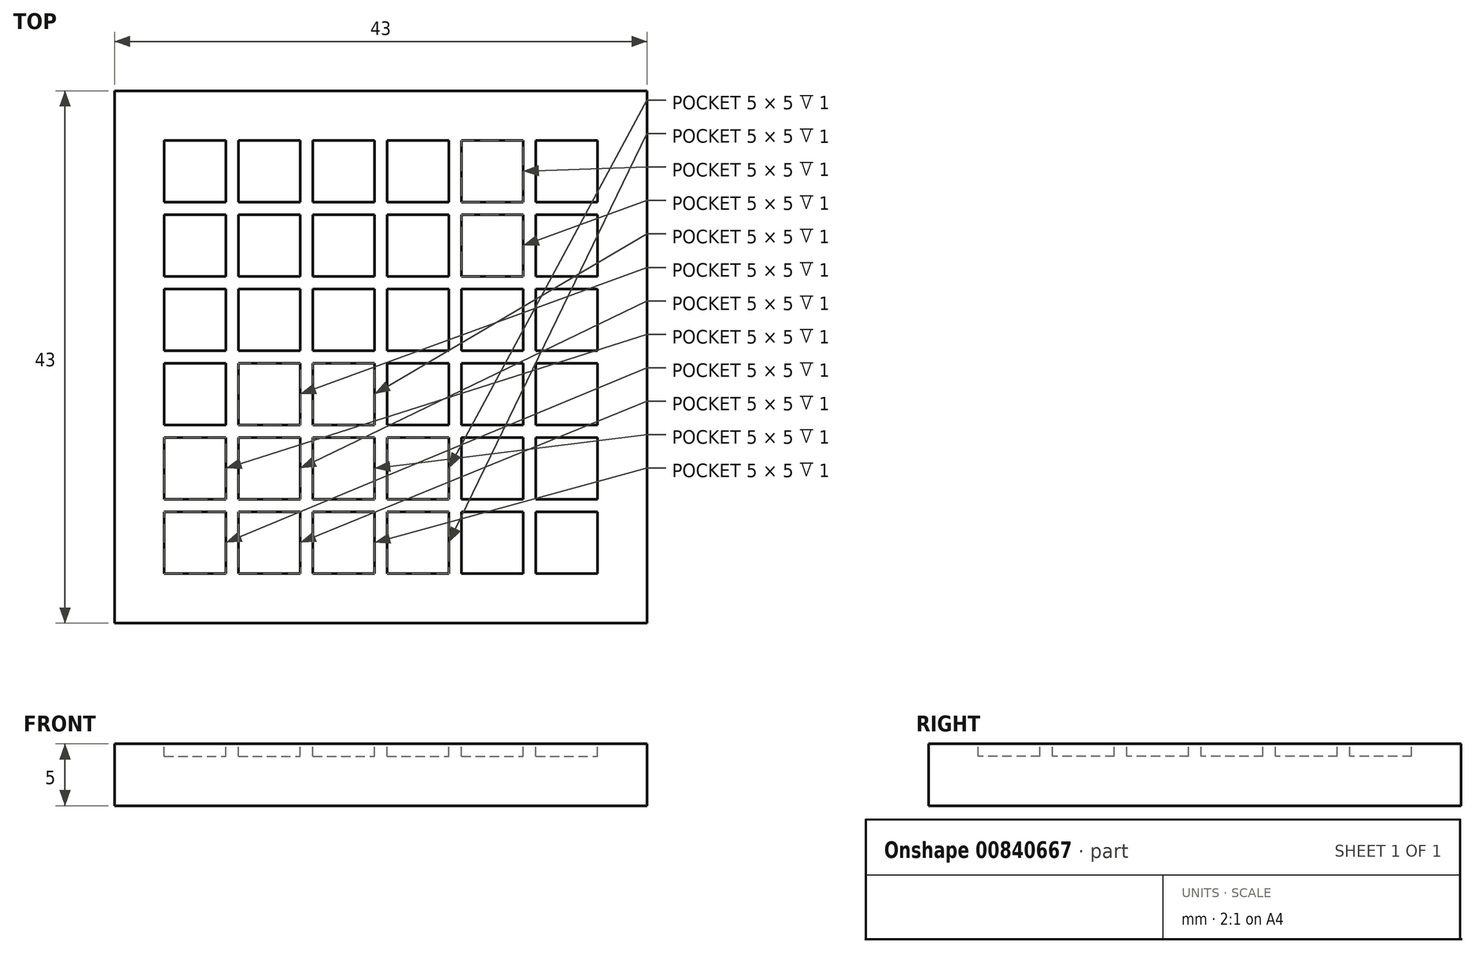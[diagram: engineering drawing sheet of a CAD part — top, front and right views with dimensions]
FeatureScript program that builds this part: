
annotation { "Feature Type Name" : "Feature", "Feature Type Description" : "" }
export const myFeature = defineFeature(function(context is Context, id is Id, definition is map)
    precondition{}
    {
        {
            var Q0;
            Q0=qCreatedBy(makeId("Top.planeOp"),FACE);
            var sketch = newSketch(context, id + "F0", { "sketchPlane" : qUnion([Q0])});
            skLineSegment(sketch, "E0.bottom", {"start": v(0, 0) * mm, "end": v(43, 0) * mm});
            skLineSegment(sketch, "E0.top", {"start": v(0, -43) * mm, "end": v(43, -43) * mm});
            skLineSegment(sketch, "E0.left", {"start": v(0, 0) * mm, "end": v(0, -43) * mm});
            skLineSegment(sketch, "E0.right", {"start": v(43, 0) * mm, "end": v(43, -43) * mm});
            skSolve(sketch);
        }
        {
            var Q0;
            Q0=makeQuery(id+"F0.imprint","IMPRINT",FACE,{"disambiguationData":[TD([[makeQuery(id+"F0.imprint","IMPRINT",EDGE,{"derivedFrom":sQuery(id+"F0.wireOp",EDGE,"E0.bottom")}),-1.0]])]});
            extrude(context, id + "F1", {"entities" : qUnion([Q0]), "depth" : 5 * mm, "offsetDistance" : 25 * mm});
        }
        {
            var Q0;
            Q0=makeQuery(id+"F1.opExtrude","CAP_FACE",FACE,{"disambiguationData":[OSD([sQuery(id+"F0.wireOp",EDGE,"E0.bottom"),sQuery(id+"F0.wireOp",EDGE,"E0.top"),sQuery(id+"F0.wireOp",EDGE,"E0.left"),sQuery(id+"F0.wireOp",EDGE,"E0.right")])],"isStart":false});
            var sketch = newSketch(context, id + "F2", { "sketchPlane" : qUnion([Q0])});
            skLineSegment(sketch, "E1.bottom", {"start": v(4, -4) * mm, "end": v(9, -4) * mm});
            skLineSegment(sketch, "E1.top", {"start": v(4, -9) * mm, "end": v(9, -9) * mm});
            skLineSegment(sketch, "E1.left", {"start": v(4, -4) * mm, "end": v(4, -9) * mm});
            skLineSegment(sketch, "E1.right", {"start": v(9, -4) * mm, "end": v(9, -9) * mm});
            skLineSegment(sketch, "E2.0.1.0", {"start": v(4, -15) * mm, "end": v(9, -15) * mm});
            skLineSegment(sketch, "E2.0.1.1", {"start": v(9, -10) * mm, "end": v(9, -15) * mm});
            skLineSegment(sketch, "E2.0.1.2", {"start": v(4, -10) * mm, "end": v(4, -15) * mm});
            skLineSegment(sketch, "E2.0.1.3", {"start": v(4, -10) * mm, "end": v(9, -10) * mm});
            skLineSegment(sketch, "E2.0.2.0", {"start": v(4, -21) * mm, "end": v(9, -21) * mm});
            skLineSegment(sketch, "E2.0.2.1", {"start": v(9, -16) * mm, "end": v(9, -21) * mm});
            skLineSegment(sketch, "E2.0.2.2", {"start": v(4, -16) * mm, "end": v(4, -21) * mm});
            skLineSegment(sketch, "E2.0.2.3", {"start": v(4, -16) * mm, "end": v(9, -16) * mm});
            skLineSegment(sketch, "E2.0.3.0", {"start": v(4, -27) * mm, "end": v(9, -27) * mm});
            skLineSegment(sketch, "E2.0.3.1", {"start": v(9, -22) * mm, "end": v(9, -27) * mm});
            skLineSegment(sketch, "E2.0.3.2", {"start": v(4, -22) * mm, "end": v(4, -27) * mm});
            skLineSegment(sketch, "E2.0.3.3", {"start": v(4, -22) * mm, "end": v(9, -22) * mm});
            skLineSegment(sketch, "E2.0.4.0", {"start": v(4, -33) * mm, "end": v(9, -33) * mm});
            skLineSegment(sketch, "E2.0.4.1", {"start": v(9, -28) * mm, "end": v(9, -33) * mm});
            skLineSegment(sketch, "E2.0.4.2", {"start": v(4, -28) * mm, "end": v(4, -33) * mm});
            skLineSegment(sketch, "E2.0.4.3", {"start": v(4, -28) * mm, "end": v(9, -28) * mm});
            skLineSegment(sketch, "E2.0.5.0", {"start": v(4, -39) * mm, "end": v(9, -39) * mm});
            skLineSegment(sketch, "E2.0.5.1", {"start": v(9, -34) * mm, "end": v(9, -39) * mm});
            skLineSegment(sketch, "E2.0.5.2", {"start": v(4, -34) * mm, "end": v(4, -39) * mm});
            skLineSegment(sketch, "E2.0.5.3", {"start": v(4, -34) * mm, "end": v(9, -34) * mm});
            skLineSegment(sketch, "E2.1.0.0", {"start": v(10, -9) * mm, "end": v(15, -9) * mm});
            skLineSegment(sketch, "E2.1.0.1", {"start": v(15, -4) * mm, "end": v(15, -9) * mm});
            skLineSegment(sketch, "E2.1.0.2", {"start": v(10, -4) * mm, "end": v(10, -9) * mm});
            skLineSegment(sketch, "E2.1.0.3", {"start": v(10, -4) * mm, "end": v(15, -4) * mm});
            skLineSegment(sketch, "E2.1.1.0", {"start": v(10, -15) * mm, "end": v(15, -15) * mm});
            skLineSegment(sketch, "E2.1.1.1", {"start": v(15, -10) * mm, "end": v(15, -15) * mm});
            skLineSegment(sketch, "E2.1.1.2", {"start": v(10, -10) * mm, "end": v(10, -15) * mm});
            skLineSegment(sketch, "E2.1.1.3", {"start": v(10, -10) * mm, "end": v(15, -10) * mm});
            skLineSegment(sketch, "E2.1.2.0", {"start": v(10, -21) * mm, "end": v(15, -21) * mm});
            skLineSegment(sketch, "E2.1.2.1", {"start": v(15, -16) * mm, "end": v(15, -21) * mm});
            skLineSegment(sketch, "E2.1.2.2", {"start": v(10, -16) * mm, "end": v(10, -21) * mm});
            skLineSegment(sketch, "E2.1.2.3", {"start": v(10, -16) * mm, "end": v(15, -16) * mm});
            skLineSegment(sketch, "E2.1.3.0", {"start": v(10, -27) * mm, "end": v(15, -27) * mm});
            skLineSegment(sketch, "E2.1.3.1", {"start": v(15, -22) * mm, "end": v(15, -27) * mm});
            skLineSegment(sketch, "E2.1.3.2", {"start": v(10, -22) * mm, "end": v(10, -27) * mm});
            skLineSegment(sketch, "E2.1.3.3", {"start": v(10, -22) * mm, "end": v(15, -22) * mm});
            skLineSegment(sketch, "E2.1.4.0", {"start": v(10, -33) * mm, "end": v(15, -33) * mm});
            skLineSegment(sketch, "E2.1.4.1", {"start": v(15, -28) * mm, "end": v(15, -33) * mm});
            skLineSegment(sketch, "E2.1.4.2", {"start": v(10, -28) * mm, "end": v(10, -33) * mm});
            skLineSegment(sketch, "E2.1.4.3", {"start": v(10, -28) * mm, "end": v(15, -28) * mm});
            skLineSegment(sketch, "E2.1.5.0", {"start": v(10, -39) * mm, "end": v(15, -39) * mm});
            skLineSegment(sketch, "E2.1.5.1", {"start": v(15, -34) * mm, "end": v(15, -39) * mm});
            skLineSegment(sketch, "E2.1.5.2", {"start": v(10, -34) * mm, "end": v(10, -39) * mm});
            skLineSegment(sketch, "E2.1.5.3", {"start": v(10, -34) * mm, "end": v(15, -34) * mm});
            skLineSegment(sketch, "E2.2.0.0", {"start": v(16, -9) * mm, "end": v(21, -9) * mm});
            skLineSegment(sketch, "E2.2.0.1", {"start": v(21, -4) * mm, "end": v(21, -9) * mm});
            skLineSegment(sketch, "E2.2.0.2", {"start": v(16, -4) * mm, "end": v(16, -9) * mm});
            skLineSegment(sketch, "E2.2.0.3", {"start": v(16, -4) * mm, "end": v(21, -4) * mm});
            skLineSegment(sketch, "E2.2.1.0", {"start": v(16, -15) * mm, "end": v(21, -15) * mm});
            skLineSegment(sketch, "E2.2.1.1", {"start": v(21, -10) * mm, "end": v(21, -15) * mm});
            skLineSegment(sketch, "E2.2.1.2", {"start": v(16, -10) * mm, "end": v(16, -15) * mm});
            skLineSegment(sketch, "E2.2.1.3", {"start": v(16, -10) * mm, "end": v(21, -10) * mm});
            skLineSegment(sketch, "E2.2.2.0", {"start": v(16, -21) * mm, "end": v(21, -21) * mm});
            skLineSegment(sketch, "E2.2.2.1", {"start": v(21, -16) * mm, "end": v(21, -21) * mm});
            skLineSegment(sketch, "E2.2.2.2", {"start": v(16, -16) * mm, "end": v(16, -21) * mm});
            skLineSegment(sketch, "E2.2.2.3", {"start": v(16, -16) * mm, "end": v(21, -16) * mm});
            skLineSegment(sketch, "E2.2.3.0", {"start": v(16, -27) * mm, "end": v(21, -27) * mm});
            skLineSegment(sketch, "E2.2.3.1", {"start": v(21, -22) * mm, "end": v(21, -27) * mm});
            skLineSegment(sketch, "E2.2.3.2", {"start": v(16, -22) * mm, "end": v(16, -27) * mm});
            skLineSegment(sketch, "E2.2.3.3", {"start": v(16, -22) * mm, "end": v(21, -22) * mm});
            skLineSegment(sketch, "E2.2.4.0", {"start": v(16, -33) * mm, "end": v(21, -33) * mm});
            skLineSegment(sketch, "E2.2.4.1", {"start": v(21, -28) * mm, "end": v(21, -33) * mm});
            skLineSegment(sketch, "E2.2.4.2", {"start": v(16, -28) * mm, "end": v(16, -33) * mm});
            skLineSegment(sketch, "E2.2.4.3", {"start": v(16, -28) * mm, "end": v(21, -28) * mm});
            skLineSegment(sketch, "E2.2.5.0", {"start": v(16, -39) * mm, "end": v(21, -39) * mm});
            skLineSegment(sketch, "E2.2.5.1", {"start": v(21, -34) * mm, "end": v(21, -39) * mm});
            skLineSegment(sketch, "E2.2.5.2", {"start": v(16, -34) * mm, "end": v(16, -39) * mm});
            skLineSegment(sketch, "E2.2.5.3", {"start": v(16, -34) * mm, "end": v(21, -34) * mm});
            skLineSegment(sketch, "E2.3.0.0", {"start": v(22, -9) * mm, "end": v(27, -9) * mm});
            skLineSegment(sketch, "E2.3.0.1", {"start": v(27, -4) * mm, "end": v(27, -9) * mm});
            skLineSegment(sketch, "E2.3.0.2", {"start": v(22, -4) * mm, "end": v(22, -9) * mm});
            skLineSegment(sketch, "E2.3.0.3", {"start": v(22, -4) * mm, "end": v(27, -4) * mm});
            skLineSegment(sketch, "E2.3.1.0", {"start": v(22, -15) * mm, "end": v(27, -15) * mm});
            skLineSegment(sketch, "E2.3.1.1", {"start": v(27, -10) * mm, "end": v(27, -15) * mm});
            skLineSegment(sketch, "E2.3.1.2", {"start": v(22, -10) * mm, "end": v(22, -15) * mm});
            skLineSegment(sketch, "E2.3.1.3", {"start": v(22, -10) * mm, "end": v(27, -10) * mm});
            skLineSegment(sketch, "E2.3.2.0", {"start": v(22, -21) * mm, "end": v(27, -21) * mm});
            skLineSegment(sketch, "E2.3.2.1", {"start": v(27, -16) * mm, "end": v(27, -21) * mm});
            skLineSegment(sketch, "E2.3.2.2", {"start": v(22, -16) * mm, "end": v(22, -21) * mm});
            skLineSegment(sketch, "E2.3.2.3", {"start": v(22, -16) * mm, "end": v(27, -16) * mm});
            skLineSegment(sketch, "E2.3.3.0", {"start": v(22, -27) * mm, "end": v(27, -27) * mm});
            skLineSegment(sketch, "E2.3.3.1", {"start": v(27, -22) * mm, "end": v(27, -27) * mm});
            skLineSegment(sketch, "E2.3.3.2", {"start": v(22, -22) * mm, "end": v(22, -27) * mm});
            skLineSegment(sketch, "E2.3.3.3", {"start": v(22, -22) * mm, "end": v(27, -22) * mm});
            skLineSegment(sketch, "E2.3.4.0", {"start": v(22, -33) * mm, "end": v(27, -33) * mm});
            skLineSegment(sketch, "E2.3.4.1", {"start": v(27, -28) * mm, "end": v(27, -33) * mm});
            skLineSegment(sketch, "E2.3.4.2", {"start": v(22, -28) * mm, "end": v(22, -33) * mm});
            skLineSegment(sketch, "E2.3.4.3", {"start": v(22, -28) * mm, "end": v(27, -28) * mm});
            skLineSegment(sketch, "E2.3.5.0", {"start": v(22, -39) * mm, "end": v(27, -39) * mm});
            skLineSegment(sketch, "E2.3.5.1", {"start": v(27, -34) * mm, "end": v(27, -39) * mm});
            skLineSegment(sketch, "E2.3.5.2", {"start": v(22, -34) * mm, "end": v(22, -39) * mm});
            skLineSegment(sketch, "E2.3.5.3", {"start": v(22, -34) * mm, "end": v(27, -34) * mm});
            skLineSegment(sketch, "E2.4.0.0", {"start": v(28, -9) * mm, "end": v(33, -9) * mm});
            skLineSegment(sketch, "E2.4.0.1", {"start": v(33, -4) * mm, "end": v(33, -9) * mm});
            skLineSegment(sketch, "E2.4.0.2", {"start": v(28, -4) * mm, "end": v(28, -9) * mm});
            skLineSegment(sketch, "E2.4.0.3", {"start": v(28, -4) * mm, "end": v(33, -4) * mm});
            skLineSegment(sketch, "E2.4.1.0", {"start": v(28, -15) * mm, "end": v(33, -15) * mm});
            skLineSegment(sketch, "E2.4.1.1", {"start": v(33, -10) * mm, "end": v(33, -15) * mm});
            skLineSegment(sketch, "E2.4.1.2", {"start": v(28, -10) * mm, "end": v(28, -15) * mm});
            skLineSegment(sketch, "E2.4.1.3", {"start": v(28, -10) * mm, "end": v(33, -10) * mm});
            skLineSegment(sketch, "E2.4.2.0", {"start": v(28, -21) * mm, "end": v(33, -21) * mm});
            skLineSegment(sketch, "E2.4.2.1", {"start": v(33, -16) * mm, "end": v(33, -21) * mm});
            skLineSegment(sketch, "E2.4.2.2", {"start": v(28, -16) * mm, "end": v(28, -21) * mm});
            skLineSegment(sketch, "E2.4.2.3", {"start": v(28, -16) * mm, "end": v(33, -16) * mm});
            skLineSegment(sketch, "E2.4.3.0", {"start": v(28, -27) * mm, "end": v(33, -27) * mm});
            skLineSegment(sketch, "E2.4.3.1", {"start": v(33, -22) * mm, "end": v(33, -27) * mm});
            skLineSegment(sketch, "E2.4.3.2", {"start": v(28, -22) * mm, "end": v(28, -27) * mm});
            skLineSegment(sketch, "E2.4.3.3", {"start": v(28, -22) * mm, "end": v(33, -22) * mm});
            skLineSegment(sketch, "E2.4.4.0", {"start": v(28, -33) * mm, "end": v(33, -33) * mm});
            skLineSegment(sketch, "E2.4.4.1", {"start": v(33, -28) * mm, "end": v(33, -33) * mm});
            skLineSegment(sketch, "E2.4.4.2", {"start": v(28, -28) * mm, "end": v(28, -33) * mm});
            skLineSegment(sketch, "E2.4.4.3", {"start": v(28, -28) * mm, "end": v(33, -28) * mm});
            skLineSegment(sketch, "E2.4.5.0", {"start": v(28, -39) * mm, "end": v(33, -39) * mm});
            skLineSegment(sketch, "E2.4.5.1", {"start": v(33, -34) * mm, "end": v(33, -39) * mm});
            skLineSegment(sketch, "E2.4.5.2", {"start": v(28, -34) * mm, "end": v(28, -39) * mm});
            skLineSegment(sketch, "E2.4.5.3", {"start": v(28, -34) * mm, "end": v(33, -34) * mm});
            skLineSegment(sketch, "E2.5.0.0", {"start": v(34, -9) * mm, "end": v(39, -9) * mm});
            skLineSegment(sketch, "E2.5.0.1", {"start": v(39, -4) * mm, "end": v(39, -9) * mm});
            skLineSegment(sketch, "E2.5.0.2", {"start": v(34, -4) * mm, "end": v(34, -9) * mm});
            skLineSegment(sketch, "E2.5.0.3", {"start": v(34, -4) * mm, "end": v(39, -4) * mm});
            skLineSegment(sketch, "E2.5.1.0", {"start": v(34, -15) * mm, "end": v(39, -15) * mm});
            skLineSegment(sketch, "E2.5.1.1", {"start": v(39, -10) * mm, "end": v(39, -15) * mm});
            skLineSegment(sketch, "E2.5.1.2", {"start": v(34, -10) * mm, "end": v(34, -15) * mm});
            skLineSegment(sketch, "E2.5.1.3", {"start": v(34, -10) * mm, "end": v(39, -10) * mm});
            skLineSegment(sketch, "E2.5.2.0", {"start": v(34, -21) * mm, "end": v(39, -21) * mm});
            skLineSegment(sketch, "E2.5.2.1", {"start": v(39, -16) * mm, "end": v(39, -21) * mm});
            skLineSegment(sketch, "E2.5.2.2", {"start": v(34, -16) * mm, "end": v(34, -21) * mm});
            skLineSegment(sketch, "E2.5.2.3", {"start": v(34, -16) * mm, "end": v(39, -16) * mm});
            skLineSegment(sketch, "E2.5.3.0", {"start": v(34, -27) * mm, "end": v(39, -27) * mm});
            skLineSegment(sketch, "E2.5.3.1", {"start": v(39, -22) * mm, "end": v(39, -27) * mm});
            skLineSegment(sketch, "E2.5.3.2", {"start": v(34, -22) * mm, "end": v(34, -27) * mm});
            skLineSegment(sketch, "E2.5.3.3", {"start": v(34, -22) * mm, "end": v(39, -22) * mm});
            skLineSegment(sketch, "E2.5.4.0", {"start": v(34, -33) * mm, "end": v(39, -33) * mm});
            skLineSegment(sketch, "E2.5.4.1", {"start": v(39, -28) * mm, "end": v(39, -33) * mm});
            skLineSegment(sketch, "E2.5.4.2", {"start": v(34, -28) * mm, "end": v(34, -33) * mm});
            skLineSegment(sketch, "E2.5.4.3", {"start": v(34, -28) * mm, "end": v(39, -28) * mm});
            skLineSegment(sketch, "E2.5.5.0", {"start": v(34, -39) * mm, "end": v(39, -39) * mm});
            skLineSegment(sketch, "E2.5.5.1", {"start": v(39, -34) * mm, "end": v(39, -39) * mm});
            skLineSegment(sketch, "E2.5.5.2", {"start": v(34, -34) * mm, "end": v(34, -39) * mm});
            skLineSegment(sketch, "E2.5.5.3", {"start": v(34, -34) * mm, "end": v(39, -34) * mm});
            skLineSegment(sketch, "E2.direction1", {"start": v(4, -9) * mm, "end": v(10, -9) * mm, "construction": true});
            skLineSegment(sketch, "E2.direction2", {"start": v(4, -9) * mm, "end": v(4, -15) * mm, "construction": true});
            skSolve(sketch);
        }
        {
            var Q0;
            Q0=makeQuery(id+"F2.imprint","IMPRINT",FACE,{"disambiguationData":[TD([[makeQuery(id+"F2.imprint","IMPRINT",EDGE,{"derivedFrom":sQuery(id+"F2.wireOp",EDGE,"E1.bottom")}),-1.0]])]});
            var Q1;
            Q1=makeQuery(id+"F2.imprint","IMPRINT",FACE,{"disambiguationData":[TD([[makeQuery(id+"F2.imprint","IMPRINT",EDGE,{"derivedFrom":sQuery(id+"F2.wireOp",EDGE,"E2.0.1.0")}),1.0]])]});
            var Q2;
            Q2=makeQuery(id+"F2.imprint","IMPRINT",FACE,{"disambiguationData":[TD([[makeQuery(id+"F2.imprint","IMPRINT",EDGE,{"derivedFrom":sQuery(id+"F2.wireOp",EDGE,"E2.0.2.0")}),1.0]])]});
            var Q3;
            Q3=makeQuery(id+"F2.imprint","IMPRINT",FACE,{"disambiguationData":[TD([[makeQuery(id+"F2.imprint","IMPRINT",EDGE,{"derivedFrom":sQuery(id+"F2.wireOp",EDGE,"E2.0.3.0")}),1.0]])]});
            var Q4;
            Q4=makeQuery(id+"F2.imprint","IMPRINT",FACE,{"disambiguationData":[TD([[makeQuery(id+"F2.imprint","IMPRINT",EDGE,{"derivedFrom":sQuery(id+"F2.wireOp",EDGE,"E2.2.0.0")}),1.0]])]});
            var Q5;
            Q5=makeQuery(id+"F2.imprint","IMPRINT",FACE,{"disambiguationData":[TD([[makeQuery(id+"F2.imprint","IMPRINT",EDGE,{"derivedFrom":sQuery(id+"F2.wireOp",EDGE,"E2.2.1.0")}),1.0]])]});
            var Q6;
            Q6=makeQuery(id+"F2.imprint","IMPRINT",FACE,{"disambiguationData":[TD([[makeQuery(id+"F2.imprint","IMPRINT",EDGE,{"derivedFrom":sQuery(id+"F2.wireOp",EDGE,"E2.2.2.0")}),1.0]])]});
            var Q7;
            Q7=makeQuery(id+"F2.imprint","IMPRINT",FACE,{"disambiguationData":[TD([[makeQuery(id+"F2.imprint","IMPRINT",EDGE,{"derivedFrom":sQuery(id+"F2.wireOp",EDGE,"E2.4.3.0")}),1.0]])]});
            var Q8;
            Q8=makeQuery(id+"F2.imprint","IMPRINT",FACE,{"disambiguationData":[TD([[makeQuery(id+"F2.imprint","IMPRINT",EDGE,{"derivedFrom":sQuery(id+"F2.wireOp",EDGE,"E2.4.4.0")}),1.0]])]});
            var Q9;
            Q9=makeQuery(id+"F2.imprint","IMPRINT",FACE,{"disambiguationData":[TD([[makeQuery(id+"F2.imprint","IMPRINT",EDGE,{"derivedFrom":sQuery(id+"F2.wireOp",EDGE,"E2.4.5.0")}),1.0]])]});
            var Q10;
            Q10=makeQuery(id+"F2.imprint","IMPRINT",FACE,{"disambiguationData":[TD([[makeQuery(id+"F2.imprint","IMPRINT",EDGE,{"derivedFrom":sQuery(id+"F2.wireOp",EDGE,"E2.5.0.0")}),1.0]])]});
            var Q11;
            Q11=makeQuery(id+"F2.imprint","IMPRINT",FACE,{"disambiguationData":[TD([[makeQuery(id+"F2.imprint","IMPRINT",EDGE,{"derivedFrom":sQuery(id+"F2.wireOp",EDGE,"E2.5.1.0")}),1.0]])]});
            var Q12;
            Q12=makeQuery(id+"F2.imprint","IMPRINT",FACE,{"disambiguationData":[TD([[makeQuery(id+"F2.imprint","IMPRINT",EDGE,{"derivedFrom":sQuery(id+"F2.wireOp",EDGE,"E2.5.2.0")}),1.0]])]});
            var Q13;
            Q13=makeQuery(id+"F2.imprint","IMPRINT",FACE,{"disambiguationData":[TD([[makeQuery(id+"F2.imprint","IMPRINT",EDGE,{"derivedFrom":sQuery(id+"F2.wireOp",EDGE,"E2.5.5.0")}),1.0]])]});
            var Q14;
            Q14=makeQuery(id+"F2.imprint","IMPRINT",FACE,{"disambiguationData":[TD([[makeQuery(id+"F2.imprint","IMPRINT",EDGE,{"derivedFrom":sQuery(id+"F2.wireOp",EDGE,"E2.5.4.0")}),1.0]])]});
            var Q15;
            Q15=makeQuery(id+"F2.imprint","IMPRINT",FACE,{"disambiguationData":[TD([[makeQuery(id+"F2.imprint","IMPRINT",EDGE,{"derivedFrom":sQuery(id+"F2.wireOp",EDGE,"E2.5.3.0")}),1.0]])]});
            var Q16;
            Q16=makeQuery(id+"F2.imprint","IMPRINT",FACE,{"disambiguationData":[TD([[makeQuery(id+"F2.imprint","IMPRINT",EDGE,{"derivedFrom":sQuery(id+"F2.wireOp",EDGE,"E2.4.2.0")}),1.0]])]});
            var Q17;
            Q17=makeQuery(id+"F2.imprint","IMPRINT",FACE,{"disambiguationData":[TD([[makeQuery(id+"F2.imprint","IMPRINT",EDGE,{"derivedFrom":sQuery(id+"F2.wireOp",EDGE,"E2.4.1.0")}),1.0]])]});
            var Q18;
            Q18=makeQuery(id+"F2.imprint","IMPRINT",FACE,{"disambiguationData":[TD([[makeQuery(id+"F2.imprint","IMPRINT",EDGE,{"derivedFrom":sQuery(id+"F2.wireOp",EDGE,"E2.4.0.0")}),1.0]])]});
            var Q19;
            Q19=makeQuery(id+"F2.imprint","IMPRINT",FACE,{"disambiguationData":[TD([[makeQuery(id+"F2.imprint","IMPRINT",EDGE,{"derivedFrom":sQuery(id+"F2.wireOp",EDGE,"E2.3.5.0")}),1.0]])]});
            var Q20;
            Q20=makeQuery(id+"F2.imprint","IMPRINT",FACE,{"disambiguationData":[TD([[makeQuery(id+"F2.imprint","IMPRINT",EDGE,{"derivedFrom":sQuery(id+"F2.wireOp",EDGE,"E2.3.4.0")}),1.0]])]});
            var Q21;
            Q21=makeQuery(id+"F2.imprint","IMPRINT",FACE,{"disambiguationData":[TD([[makeQuery(id+"F2.imprint","IMPRINT",EDGE,{"derivedFrom":sQuery(id+"F2.wireOp",EDGE,"E2.3.3.0")}),1.0]])]});
            var Q22;
            Q22=makeQuery(id+"F2.imprint","IMPRINT",FACE,{"disambiguationData":[TD([[makeQuery(id+"F2.imprint","IMPRINT",EDGE,{"derivedFrom":sQuery(id+"F2.wireOp",EDGE,"E2.3.2.0")}),1.0]])]});
            var Q23;
            Q23=makeQuery(id+"F2.imprint","IMPRINT",FACE,{"disambiguationData":[TD([[makeQuery(id+"F2.imprint","IMPRINT",EDGE,{"derivedFrom":sQuery(id+"F2.wireOp",EDGE,"E2.3.1.0")}),1.0]])]});
            var Q24;
            Q24=makeQuery(id+"F2.imprint","IMPRINT",FACE,{"disambiguationData":[TD([[makeQuery(id+"F2.imprint","IMPRINT",EDGE,{"derivedFrom":sQuery(id+"F2.wireOp",EDGE,"E2.3.0.0")}),1.0]])]});
            var Q25;
            Q25=makeQuery(id+"F2.imprint","IMPRINT",FACE,{"disambiguationData":[TD([[makeQuery(id+"F2.imprint","IMPRINT",EDGE,{"derivedFrom":sQuery(id+"F2.wireOp",EDGE,"E2.2.5.0")}),1.0]])]});
            var Q26;
            Q26=makeQuery(id+"F2.imprint","IMPRINT",FACE,{"disambiguationData":[TD([[makeQuery(id+"F2.imprint","IMPRINT",EDGE,{"derivedFrom":sQuery(id+"F2.wireOp",EDGE,"E2.2.4.0")}),1.0]])]});
            var Q27;
            Q27=makeQuery(id+"F2.imprint","IMPRINT",FACE,{"disambiguationData":[TD([[makeQuery(id+"F2.imprint","IMPRINT",EDGE,{"derivedFrom":sQuery(id+"F2.wireOp",EDGE,"E2.1.5.0")}),1.0]])]});
            var Q28;
            Q28=makeQuery(id+"F2.imprint","IMPRINT",FACE,{"disambiguationData":[TD([[makeQuery(id+"F2.imprint","IMPRINT",EDGE,{"derivedFrom":sQuery(id+"F2.wireOp",EDGE,"E2.0.5.0")}),1.0]])]});
            var Q29;
            Q29=makeQuery(id+"F2.imprint","IMPRINT",FACE,{"disambiguationData":[TD([[makeQuery(id+"F2.imprint","IMPRINT",EDGE,{"derivedFrom":sQuery(id+"F2.wireOp",EDGE,"E2.0.4.0")}),1.0]])]});
            var Q30;
            Q30=makeQuery(id+"F2.imprint","IMPRINT",FACE,{"disambiguationData":[TD([[makeQuery(id+"F2.imprint","IMPRINT",EDGE,{"derivedFrom":sQuery(id+"F2.wireOp",EDGE,"E2.1.4.0")}),1.0]])]});
            var Q31;
            Q31=makeQuery(id+"F2.imprint","IMPRINT",FACE,{"disambiguationData":[TD([[makeQuery(id+"F2.imprint","IMPRINT",EDGE,{"derivedFrom":sQuery(id+"F2.wireOp",EDGE,"E2.1.3.0")}),1.0]])]});
            var Q32;
            Q32=makeQuery(id+"F2.imprint","IMPRINT",FACE,{"disambiguationData":[TD([[makeQuery(id+"F2.imprint","IMPRINT",EDGE,{"derivedFrom":sQuery(id+"F2.wireOp",EDGE,"E2.2.3.0")}),1.0]])]});
            var Q33;
            Q33=makeQuery(id+"F2.imprint","IMPRINT",FACE,{"disambiguationData":[TD([[makeQuery(id+"F2.imprint","IMPRINT",EDGE,{"derivedFrom":sQuery(id+"F2.wireOp",EDGE,"E2.1.2.0")}),1.0]])]});
            var Q34;
            Q34=makeQuery(id+"F2.imprint","IMPRINT",FACE,{"disambiguationData":[TD([[makeQuery(id+"F2.imprint","IMPRINT",EDGE,{"derivedFrom":sQuery(id+"F2.wireOp",EDGE,"E2.1.1.0")}),1.0]])]});
            var Q35;
            Q35=makeQuery(id+"F2.imprint","IMPRINT",FACE,{"disambiguationData":[TD([[makeQuery(id+"F2.imprint","IMPRINT",EDGE,{"derivedFrom":sQuery(id+"F2.wireOp",EDGE,"E2.1.0.0")}),1.0]])]});
            extrude(context, id + "F3", {"entities" : qUnion([Q0, Q1, Q2, Q3, Q4, Q5, Q6, Q7, Q8, Q9, Q10, Q11, Q12, Q13, Q14, Q15, Q16, Q17, Q18, Q19, Q20, Q21, Q22, Q23, Q24, Q25, Q26, Q27, Q28, Q29, Q30, Q31, Q32, Q33, Q34, Q35]), "operationType" : NewBodyOperationType.REMOVE, "oppositeDirection" : true, "depth" : 1 * mm, "offsetDistance" : 25 * mm});
        }
    });
